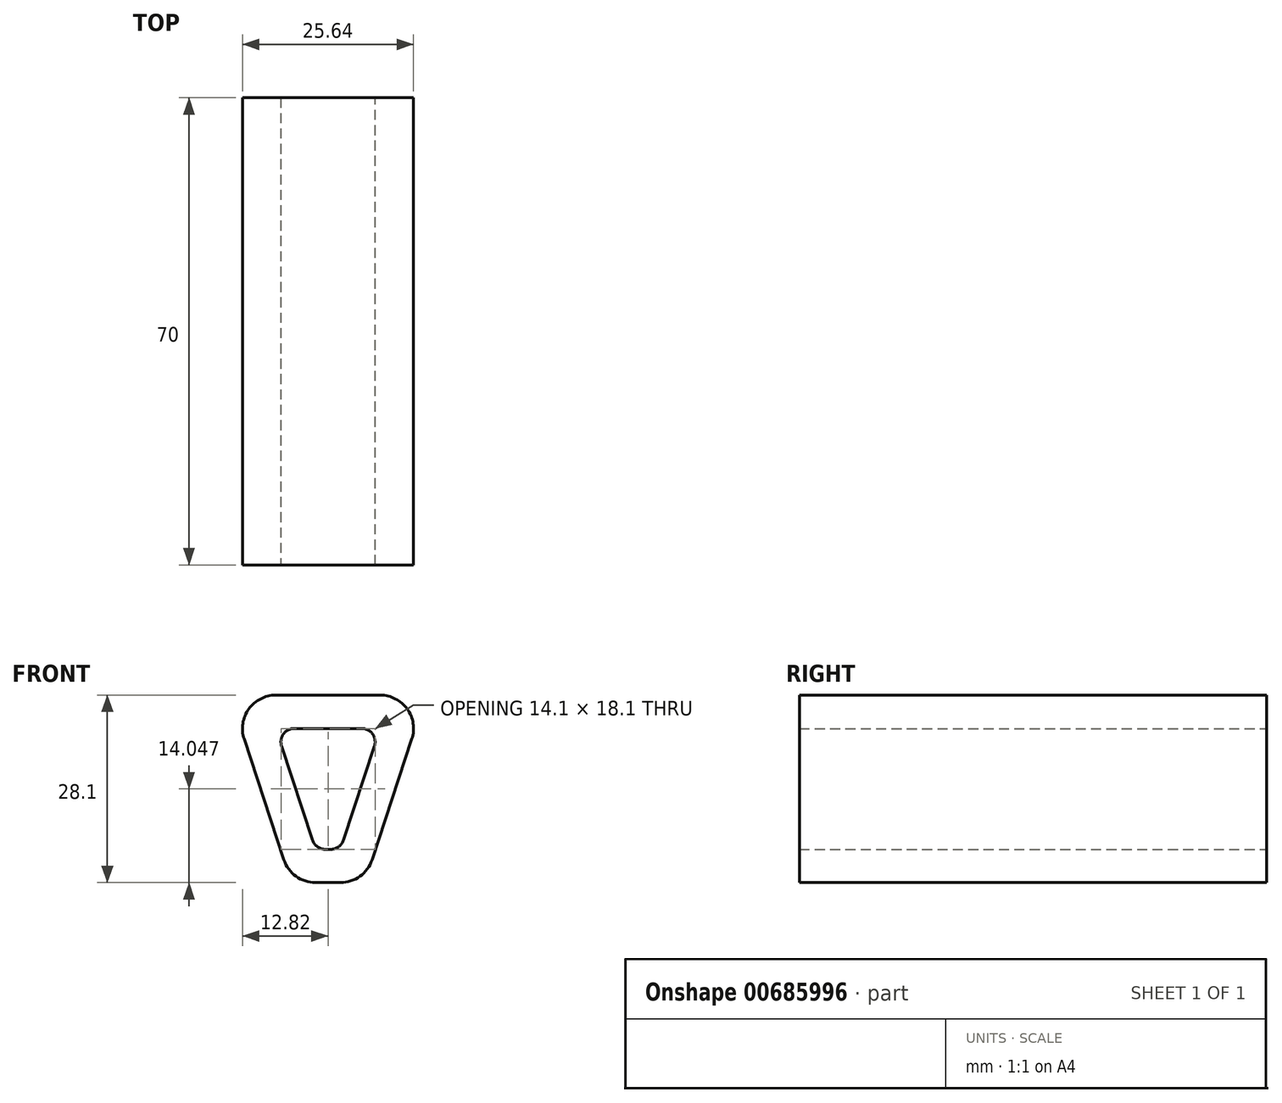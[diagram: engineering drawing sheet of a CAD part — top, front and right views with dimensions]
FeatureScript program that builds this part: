
annotation { "Feature Type Name" : "Feature", "Feature Type Description" : "" }
export const myFeature = defineFeature(function(context is Context, id is Id, definition is map)
    precondition{}
    {
        {
            var Q0;
            Q0=qCreatedBy(makeId("Front.planeOp"),FACE);
            var sketch = newSketch(context, id + "F0", { "sketchPlane" : qUnion([Q0])});
            skLineSegment(sketch, "E0", {"start": v(0, 12.05) * mm, "end": v(7.82, 12.05) * mm});
            skLineSegment(sketch, "E1", {"start": v(7.82, 12.05) * mm, "end": v(1.86, -6.05) * mm});
            skLineSegment(sketch, "E2", {"start": v(1.86, -6.05) * mm, "end": v(0, -6.05) * mm});
            skLineSegment(sketch, "E3.MirrorCS", {"start": v(0, 12.05) * mm, "end": v(-7.82, 12.05) * mm});
            skLineSegment(sketch, "E4.MirrorCS", {"start": v(-7.82, 12.05) * mm, "end": v(-1.86, -6.05) * mm});
            skLineSegment(sketch, "E5.MirrorCS", {"start": v(-1.86, -6.05) * mm, "end": v(0, -6.05) * mm});
            skLineSegment(sketch, "E6.0", {"start": v(0, 17.05) * mm, "end": v(14.73, 17.05) * mm});
            skLineSegment(sketch, "E6.1", {"start": v(-14.73, 17.05) * mm, "end": v(-5.48, -11.05) * mm});
            skLineSegment(sketch, "E6.2", {"start": v(-5.48, -11.05) * mm, "end": v(0, -11.05) * mm});
            skLineSegment(sketch, "E6.3", {"start": v(0, 17.05) * mm, "end": v(-14.73, 17.05) * mm});
            skLineSegment(sketch, "E6.4", {"start": v(5.48, -11.05) * mm, "end": v(0, -11.05) * mm});
            skLineSegment(sketch, "E6.5", {"start": v(14.73, 17.05) * mm, "end": v(5.48, -11.05) * mm});
            skSolve(sketch);
        }
        {
            var Q0;
            Q0 = qSketchRegion(id + "F0", true);
            extrude(context, id + "F1", {"entities" : qUnion([Q0]), "depth" : 70 * mm, "offsetDistance" : 25 * mm});
        }
        {
            var Q0;
            Q0=makeQuery(id+"F1.opExtrude","SWEPT_EDGE",EDGE,{"disambiguationData":[OSD([sQuery(id+"F0.wireOp",EDGE,"E6.0"),sQuery(id+"F0.wireOp",EDGE,"E6.5")])]});
            var Q1;
            Q1=makeQuery(id+"F1.opExtrude","SWEPT_EDGE",EDGE,{"disambiguationData":[OSD([sQuery(id+"F0.wireOp",EDGE,"E6.4"),sQuery(id+"F0.wireOp",EDGE,"E6.5")])]});
            var Q2;
            Q2=makeQuery(id+"F1.opExtrude","SWEPT_EDGE",EDGE,{"disambiguationData":[OSD([sQuery(id+"F0.wireOp",EDGE,"E6.1"),sQuery(id+"F0.wireOp",EDGE,"E6.2")])]});
            var Q3;
            Q3=makeQuery(id+"F1.opExtrude","SWEPT_EDGE",EDGE,{"disambiguationData":[OSD([sQuery(id+"F0.wireOp",EDGE,"E6.1"),sQuery(id+"F0.wireOp",EDGE,"E6.3")])]});
            fillet(context, id + "F2", {"entities" : qUnion([Q0, Q1, Q2, Q3]), "radius" : 5 * mm, "tangentPropagation" : true, "allowEdgeOverflow" : false});
        }
        {
            var Q0;
            Q0=makeQuery(id+"F1.opExtrude","SWEPT_EDGE",EDGE,{"disambiguationData":[OSD([sQuery(id+"F0.wireOp",EDGE,"E4.MirrorCS"),sQuery(id+"F0.wireOp",EDGE,"E5.MirrorCS")])]});
            var Q1;
            Q1=makeQuery(id+"F1.opExtrude","SWEPT_EDGE",EDGE,{"disambiguationData":[OSD([sQuery(id+"F0.wireOp",EDGE,"E1"),sQuery(id+"F0.wireOp",EDGE,"E2")])]});
            var Q2;
            Q2=makeQuery(id+"F1.opExtrude","SWEPT_EDGE",EDGE,{"disambiguationData":[OSD([sQuery(id+"F0.wireOp",EDGE,"E0"),sQuery(id+"F0.wireOp",EDGE,"E1")])]});
            var Q3;
            Q3=makeQuery(id+"F1.opExtrude","SWEPT_EDGE",EDGE,{"disambiguationData":[OSD([sQuery(id+"F0.wireOp",EDGE,"E3.MirrorCS"),sQuery(id+"F0.wireOp",EDGE,"E4.MirrorCS")])]});
            fillet(context, id + "F3", {"entities" : qUnion([Q0, Q1, Q2, Q3]), "radius" : 2 * mm, "tangentPropagation" : true, "allowEdgeOverflow" : false});
        }
    });
